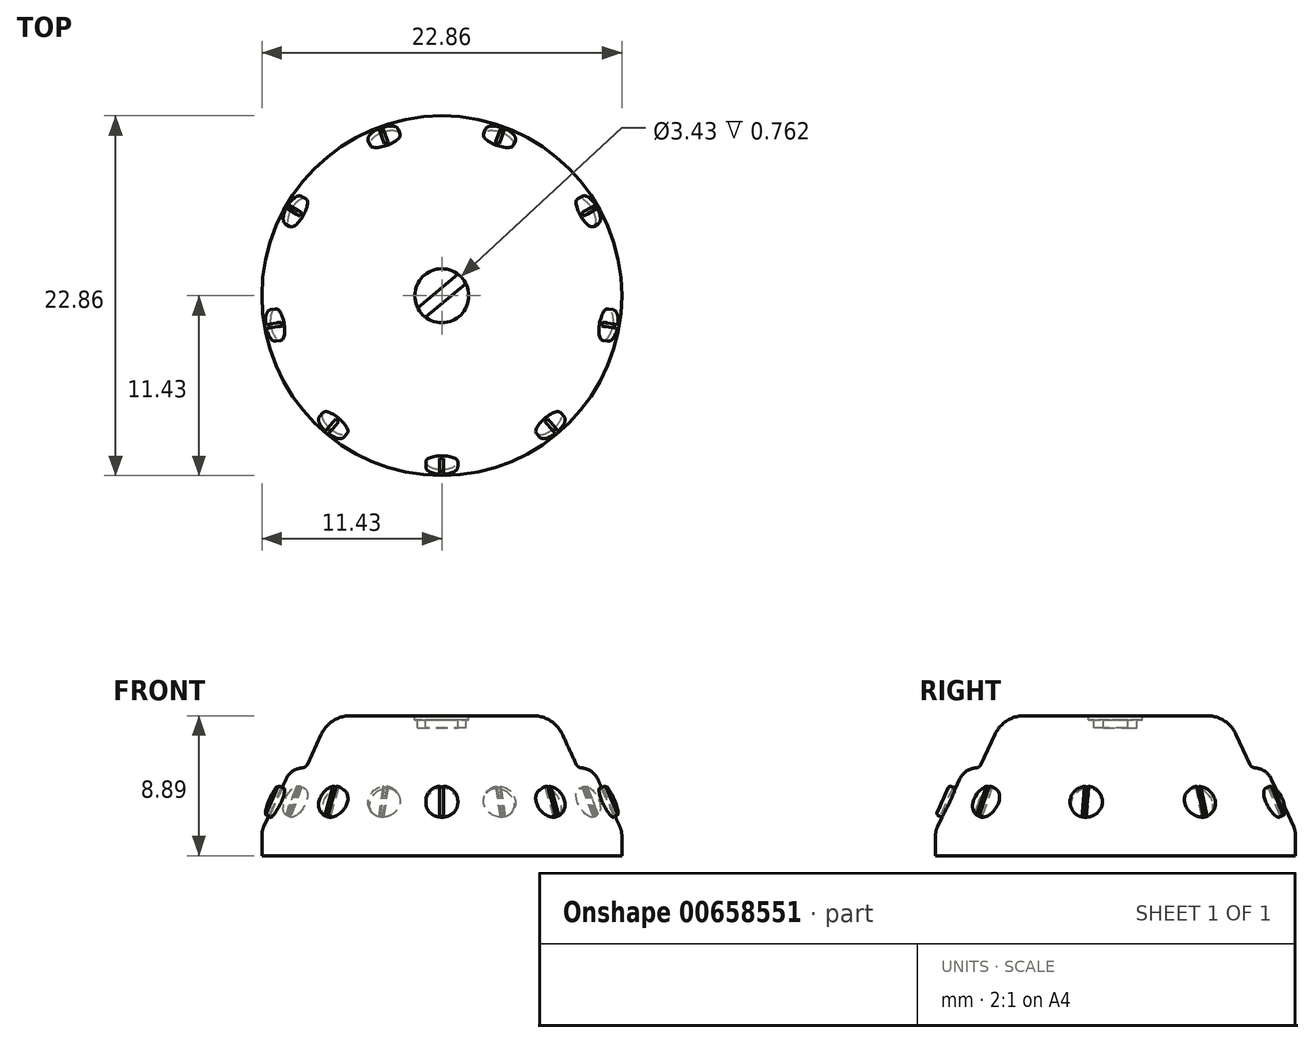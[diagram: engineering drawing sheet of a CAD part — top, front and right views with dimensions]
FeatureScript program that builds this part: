
annotation { "Feature Type Name" : "Feature", "Feature Type Description" : "" }
export const myFeature = defineFeature(function(context is Context, id is Id, definition is map)
    precondition{}
    {
        {
            var Q0;
            Q0=qCreatedBy(makeId("Front.planeOp"),FACE);
            var sketch = newSketch(context, id + "F0", { "sketchPlane" : qUnion([Q0])});
            skLineSegment(sketch, "E0", {"start": v(0, 0) * mm, "end": v(-11.43, 0) * mm});
            skLineSegment(sketch, "E1", {"start": v(-11.43, 0) * mm, "end": v(-11.43, 1.59) * mm});
            skLineSegment(sketch, "E2", {"start": v(-11.43, 1.59) * mm, "end": v(-9.56, 5.59) * mm});
            skLineSegment(sketch, "E3", {"start": v(-9.56, 5.59) * mm, "end": v(-8.64, 5.59) * mm});
            skLineSegment(sketch, "E4", {"start": v(-8.64, 5.59) * mm, "end": v(-7.11, 8.9) * mm});
            skLineSegment(sketch, "E5", {"start": v(-7.11, 8.9) * mm, "end": v(0, 8.9) * mm});
            skLineSegment(sketch, "E6", {"start": v(0, 8.9) * mm, "end": v(0, 0) * mm});
            skSolve(sketch);
        }
        {
            var Q0;
            Q0=makeQuery(id+"F0.imprint","IMPRINT",FACE,{"disambiguationData":[TD([[makeQuery(id+"F0.imprint","IMPRINT",EDGE,{"derivedFrom":sQuery(id+"F0.wireOp",EDGE,"E0")}),-1.0]])]});
            var Q1;
            Q1=sQuery(id+"F0.wireOp",EDGE,"E6");
            revolve(context, id + "F1", {"entities" : qUnion([Q0]), "axis" : qUnion([Q1]), "revolveType" : RevolveType.FULL});
        }
        {
            var Q0;
            Q0=makeQuery(id+"F1.opRevolve","SWEPT_EDGE",EDGE,{"disambiguationData":[OSD([sQuery(id+"F0.wireOp",EDGE,"E2"),sQuery(id+"F0.wireOp",EDGE,"E3")])]});
            var Q1;
            Q1=makeQuery(id+"F1.opRevolve","SWEPT_EDGE",EDGE,{"disambiguationData":[OSD([sQuery(id+"F0.wireOp",EDGE,"E1"),sQuery(id+"F0.wireOp",EDGE,"E2")])]});
            fillet(context, id + "F2", {"entities" : qUnion([Q0, Q1]), "radius" : 1.27 * mm, "tangentPropagation" : true, "allowEdgeOverflow" : false});
        }
        {
            var Q0;
            Q0=makeQuery(id+"F1.opRevolve","SWEPT_EDGE",EDGE,{"disambiguationData":[OSD([sQuery(id+"F0.wireOp",EDGE,"E4"),sQuery(id+"F0.wireOp",EDGE,"E5")])]});
            fillet(context, id + "F3", {"entities" : qUnion([Q0]), "radius" : 2.03 * mm, "tangentPropagation" : true, "allowEdgeOverflow" : false});
        }
        {
            var Q0;
            Q0=makeQuery(id+"F1.opRevolve","SWEPT_EDGE",EDGE,{"disambiguationData":[OSD([sQuery(id+"F0.wireOp",EDGE,"E3"),sQuery(id+"F0.wireOp",EDGE,"E4")])]});
            fillet(context, id + "F4", {"entities" : qUnion([Q0]), "radius" : 0.38 * mm, "tangentPropagation" : true, "allowEdgeOverflow" : false});
        }
        {
            var Q0;
            Q0=makeQuery(id+"F1.opRevolve","SWEPT_FACE",FACE,{"disambiguationData":[OSD([sQuery(id+"F0.wireOp",EDGE,"E5")])]});
            var sketch = newSketch(context, id + "F5", { "sketchPlane" : qUnion([Q0])});
            skCircle(sketch, "E7", {"center": v(0, 0) * mm, "radius": 1.71 * mm});
            skSolve(sketch);
        }
        {
            var Q0;
            Q0 = qSketchRegion(id + "F5", true);
            extrude(context, id + "F6", {"entities" : qUnion([Q0]), "operationType" : NewBodyOperationType.REMOVE, "oppositeDirection" : true, "depth" : 0.25 * mm, "offsetDistance" : 25.4 * mm});
        }
        {
            var Q0;
            Q0=qCreatedBy(makeId("Right.planeOp"),FACE);
            var sketch = newSketch(context, id + "F7", { "sketchPlane" : qUnion([Q0])});
            skLineSegment(sketch, "E8", {"start": v(-12.11, 0.92) * mm, "end": v(-9.8, 6.22) * mm});
            skSolve(sketch);
        }
        {
            var Q0;
            Q0=sQuery(id+"F7.wireOp",EDGE,"E8");
            cPlane(context, id + "F8", {"entities" : qUnion([Q0]), "cplaneType" : CPlaneType.LINE_ANGLE, "offset" : 25.4 * mm, "angle" : 90 * degree, "width" : 152.4 * mm, "height" : 152.4 * mm});
        }
        {
            var Q0;
            Q0=qCreatedBy(id+"F8.planeOp",FACE);
            var sketch = newSketch(context, id + "F9", { "sketchPlane" : qUnion([Q0])});
            skCircle(sketch, "E9", {"center": v(0, -1.15) * mm, "radius": 1.02 * mm});
            skSolve(sketch);
        }
        {
            var Q0;
            Q0 = qSketchRegion(id + "F9", true);
            extrude(context, id + "F10", {"entities" : qUnion([Q0]), "operationType" : NewBodyOperationType.ADD, "depth" : 2.54 * mm, "offsetDistance" : 25.4 * mm});
        }
        {
            var Q0;
            Q0=makeQuery(id+"F10.opExtrude","CAP_EDGE",EDGE,{"disambiguationData":[OSD([sQuery(id+"F9.wireOp",EDGE,"E9")])],"isStart":true});
            fillet(context, id + "F11", {"entities" : qUnion([Q0]), "radius" : 0.13 * mm, "tangentPropagation" : true, "allowEdgeOverflow" : false});
        }
        {
            var Q0;
            Q0=makeQuery(id+"F10.opExtrude","CAP_FACE",FACE,{"disambiguationData":[OSD([sQuery(id+"F9.wireOp",EDGE,"E9")])],"isStart":true});
            var sketch = newSketch(context, id + "F12", { "sketchPlane" : qUnion([Q0])});
            skLineSegment(sketch, "E10.bottom", {"start": v(-0.13, 0.14) * mm, "end": v(0.13, 0.14) * mm});
            skLineSegment(sketch, "E10.top", {"start": v(-0.13, -2.4) * mm, "end": v(0.13, -2.4) * mm});
            skLineSegment(sketch, "E10.left", {"start": v(-0.13, 0.14) * mm, "end": v(-0.13, -2.4) * mm});
            skLineSegment(sketch, "E10.right", {"start": v(0.13, 0.14) * mm, "end": v(0.13, -2.4) * mm});
            skSolve(sketch);
        }
        {
            var Q0;
            Q0 = qSketchRegion(id + "F12", true);
            extrude(context, id + "F13", {"entities" : qUnion([Q0]), "operationType" : NewBodyOperationType.REMOVE, "oppositeDirection" : true, "depth" : 0.25 * mm, "offsetDistance" : 25.4 * mm});
        }
        {
            var Q0;
            Q0=makeQuery(id+"F6.boolean.opBoolean","COPY",FACE,{"derivedFrom":makeQuery(id+"F6.opExtrude","CAP_FACE",FACE,{"disambiguationData":[OSD([sQuery(id+"F5.wireOp",EDGE,"E7")])],"isStart":false})});
            var sketch = newSketch(context, id + "F14", { "sketchPlane" : qUnion([Q0])});
            skArc(sketch, "E11", {"start": v(-1.53, -0.78) * mm, "mid": v(-1.32, -1.1) * mm, "end": v(-1.04, -1.36) * mm});
            skLineSegment(sketch, "E12", {"start": v(-1.53, -0.78) * mm, "end": v(1.04, 1.36) * mm});
            skLineSegment(sketch, "E13", {"start": v(1.53, 0.78) * mm, "end": v(-1.04, -1.36) * mm});
            skArc(sketch, "E14.trimOffspring", {"start": v(1.53, 0.78) * mm, "mid": v(1.32, 1.1) * mm, "end": v(1.04, 1.36) * mm});
            skSolve(sketch);
        }
        {
            var Q0;
            Q0=makeQuery(id+"F1.opRevolve","SWEPT_BODY",BODY,{"disambiguationData":[OSD([sQuery(id+"F0.wireOp",EDGE,"E0"),sQuery(id+"F0.wireOp",EDGE,"E1"),sQuery(id+"F0.wireOp",EDGE,"E2"),sQuery(id+"F0.wireOp",EDGE,"E3"),sQuery(id+"F0.wireOp",EDGE,"E4"),sQuery(id+"F0.wireOp",EDGE,"E5"),sQuery(id+"F0.wireOp",EDGE,"E6")])]});
            var Q1;
            Q1=makeQuery(id+"F1.opRevolve","SWEPT_EDGE",EDGE,{"disambiguationData":[OSD([sQuery(id+"F0.wireOp",EDGE,"E0"),sQuery(id+"F0.wireOp",EDGE,"E1")])]});
            circularPattern(context, id + "F15", {"operationType" : NewBodyOperationType.ADD, "entities" : qUnion([Q0]), "axis" : qUnion([Q1]), "angle" : 360 * degree, "instanceCount" : 9, "equalSpace" : true});
        }
        {
            var Q0;
            Q0 = qSketchRegion(id + "F14", true);
            extrude(context, id + "F16", {"entities" : qUnion([Q0]), "operationType" : NewBodyOperationType.REMOVE, "oppositeDirection" : true, "depth" : 0.5 * mm, "offsetDistance" : 25.4 * mm});
        }
    });
